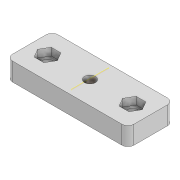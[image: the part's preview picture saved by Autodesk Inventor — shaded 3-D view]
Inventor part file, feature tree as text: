
AUTODESK INVENTOR PART (.ipt)
format: ipt  version: 2020 (Build 240168000, 168)  size: 134,656 bytes
history: native  units: mm
features: extrude x5, sketch x5, mirror x2, fillet x1, plane x1
ambient origin geometry x8: Origin, YZ Plane, XZ Plane, XY Plane, X Axis, Y Axis, Z Axis, Center Point
bodies: Solid1 (feature_tree)
feature tree (14):
  extrude  "Extrusion1"  Depth=15.0mm
  fillet  "Fillet1"  Radius=6.0mm
  plane  "Work Plane1"
  extrude  "Extrusion3"  [1 undecoded]
  extrude  "Extrusion4"  Depth=6.0mm TaperAngle=0.0deg
  extrude  "Extrusion5"  Depth=2.5mm
  extrude  "Extrusion6"  Depth=2.5mm TaperAngle=0.0deg
  mirror  "Mirror1"
  mirror  "Mirror2"
  sketch  "Sketch1"  dims[d0=40.0mm d1=15.0mm d2=6.0mm d3=0.0mm]
  sketch  "Sketch2"  dims[d4=2.0mm d5=-20.0mm]
  sketch  "Sketch4"  dims[d9=3.6mm d10=6.0mm d11=0.0mm]
  sketch  "Sketch5"  dims[d13=2.5mm d14=0.0mm d15=3.6mm]
  sketch  "Sketch6"  dims[d16=6.0mm d17=0.0mm d19=2.5mm d20=0.0mm]
note: 1 required parameter value undecoded (feature->parameter linkage not recoverable at this tier; creation-order binding heuristic only, values carry confidence <= 0.55)
